# Revit family: SCI_FL_DK25-L6 CN
name_source: partatom
category: Generic Models
units: mm (PartAtom-declared; Revit-internal decimal feet)

## family parameters
Always vertical = Yes
Can host rebar = No
Cut with Voids When Loaded = No
Host = Floor
Part Type = Normal
Room Calculation Point = No
Round Connector Dimension = Use Diameter
Shared = No

## types (1)
- SCI_FL_DK25-L6 CN
    Catalog = https://bit.ly
    Category = พื้น
    D = 25 mm  [stored 0.082021 ft]
    Instruction Video = https://youtu.be
    L = 2800 mm  [stored 9.18635 ft]
    Manufacturer = SCI WOOD
    Material = Teak
    Material main = WPC
    No. of pc / sq.m. = 2.55
    Product Description = https://bit.ly
    Product Type = ไม้ระแนง ภายนอก(Decking Outdoor)
    Product code = DK25-L6 CN T
    Series = ไม้พื้นตันแคนนาดา หน้า 6"(Decking Luxury Elegance Prestige 6")
    Sub-Category = ไม้พื้น
    W = 140 mm  [stored 0.459318 ft]
    Weight/Sheet (kg) = 12

note: [stored X ft] marks values corroborated as IEEE doubles in the binary element streams (Revit-internal decimal feet)

## geometry (parser evidence)
native form markers: Sweep x2
no freeform markers — native parametric forms only
